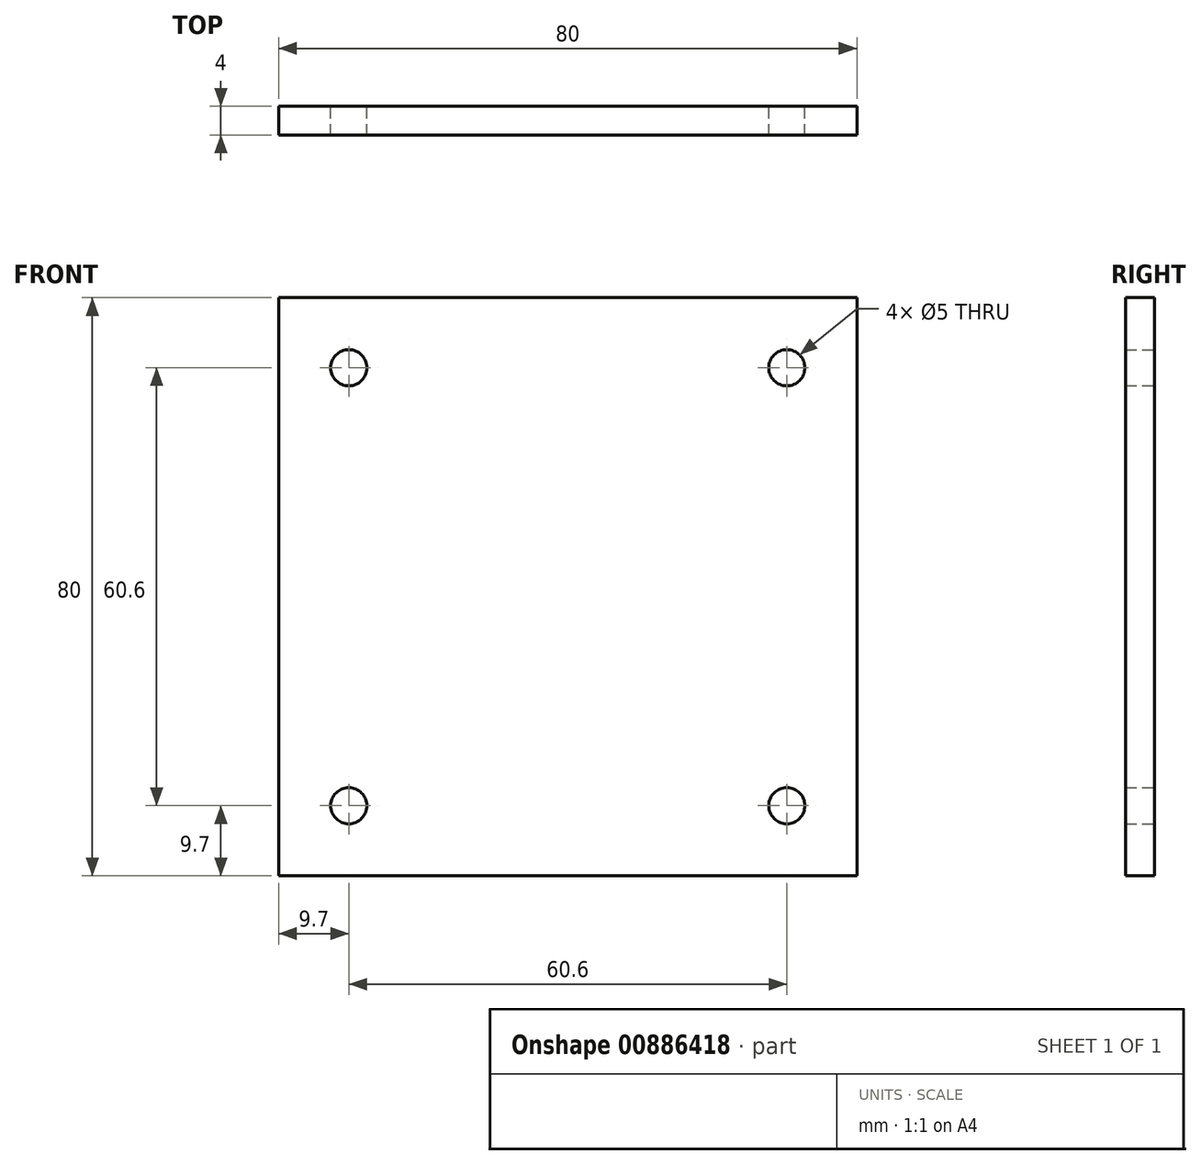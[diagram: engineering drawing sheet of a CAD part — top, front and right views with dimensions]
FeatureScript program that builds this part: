
annotation { "Feature Type Name" : "Feature", "Feature Type Description" : "" }
export const myFeature = defineFeature(function(context is Context, id is Id, definition is map)
    precondition{}
    {
        {
            var Q0;
            Q0=qCreatedBy(makeId("Front.planeOp"),FACE);
            var sketch = newSketch(context, id + "F0", { "sketchPlane" : qUnion([Q0])});
            skLineSegment(sketch, "E0.bottom", {"start": v(40, 40) * mm, "end": v(-40, 40) * mm});
            skLineSegment(sketch, "E0.top", {"start": v(40, -40) * mm, "end": v(-40, -40) * mm});
            skLineSegment(sketch, "E0.left", {"start": v(40, 40) * mm, "end": v(40, -40) * mm});
            skLineSegment(sketch, "E0.right", {"start": v(-40, 40) * mm, "end": v(-40, -40) * mm});
            skPoint(sketch, "E0.middle", {"position": v(0, 0) * mm});
            skLineSegment(sketch, "E1", {"start": v(30.3, 40) * mm, "end": v(30.3, -40) * mm, "construction": true});
            skLineSegment(sketch, "E2", {"start": v(40, 30.3) * mm, "end": v(-40, 30.3) * mm, "construction": true});
            skLineSegment(sketch, "E3.MirrorCS", {"start": v(-30.3, 40) * mm, "end": v(-30.3, -40) * mm, "construction": true});
            skLineSegment(sketch, "E4.MirrorCS", {"start": v(40, -30.3) * mm, "end": v(-40, -30.3) * mm, "construction": true});
            skPoint(sketch, "E5", {"position": v(-30.3, 30.3) * mm});
            skPoint(sketch, "E6", {"position": v(30.3, 30.3) * mm});
            skPoint(sketch, "E7", {"position": v(30.3, -30.3) * mm});
            skPoint(sketch, "E8", {"position": v(-30.3, -30.3) * mm});
            skSolve(sketch);
        }
        {
            var Q0;
            Q0 = qSketchRegion(id + "F0", true);
            extrude(context, id + "F1", {"entities" : qUnion([Q0]), "depth" : 4 * mm, "offsetDistance" : 25 * mm});
        }
        {
            var Q0;
            Q0=sQuery(id+"F0.wireOp",VERTEX,"E8");
            var Q1;
            Q1=sQuery(id+"F0.wireOp",VERTEX,"E7");
            var Q2;
            Q2=sQuery(id+"F0.wireOp",VERTEX,"E6");
            var Q3;
            Q3=sQuery(id+"F0.wireOp",VERTEX,"E5");
            var Q4;
            Q4=makeQuery(id+"F1.opExtrude","SWEPT_BODY",BODY,{"disambiguationData":[OSD([sQuery(id+"F0.wireOp",EDGE,"E0.bottom"),sQuery(id+"F0.wireOp",EDGE,"E0.top"),sQuery(id+"F0.wireOp",EDGE,"E0.left"),sQuery(id+"F0.wireOp",EDGE,"E0.right")])]});
            hole(context, id + "F2", {"style" : HoleStyle.SIMPLE, "endStyle" : HoleEndStyle.THROUGH, "oppositeDirection" : true, "holeDiameter" : 5 * mm, "majorDiameter" : 5 * mm, "isTappedThrough" : true, "tappedDepth" : 12 * mm, "tapClearance" : 3, "locations" : qUnion([Q0, Q1, Q2, Q3]), "scope" : qUnion([Q4])});
        }
    });
